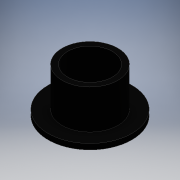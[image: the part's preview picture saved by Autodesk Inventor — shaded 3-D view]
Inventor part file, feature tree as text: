
AUTODESK INVENTOR PART (.ipt)
format: ipt  version: 2016 (Build 200138000, 138)  size: 102,912 bytes
history: native  units: mm
features: extrude x2, other x1, sketch x1
ambient origin geometry x8: Origin, YZ Plane, XZ Plane, XY Plane, X Axis, Y Axis, Z Axis, Center Point
bodies: Body1 (feature_tree)
feature tree (4):
  other  "ソリッド1"
  sketch  "スケッチ1"
  extrude  "押し出し1"  Depth=15.0mm
  extrude  "押し出し2"  Depth=10.0mm
